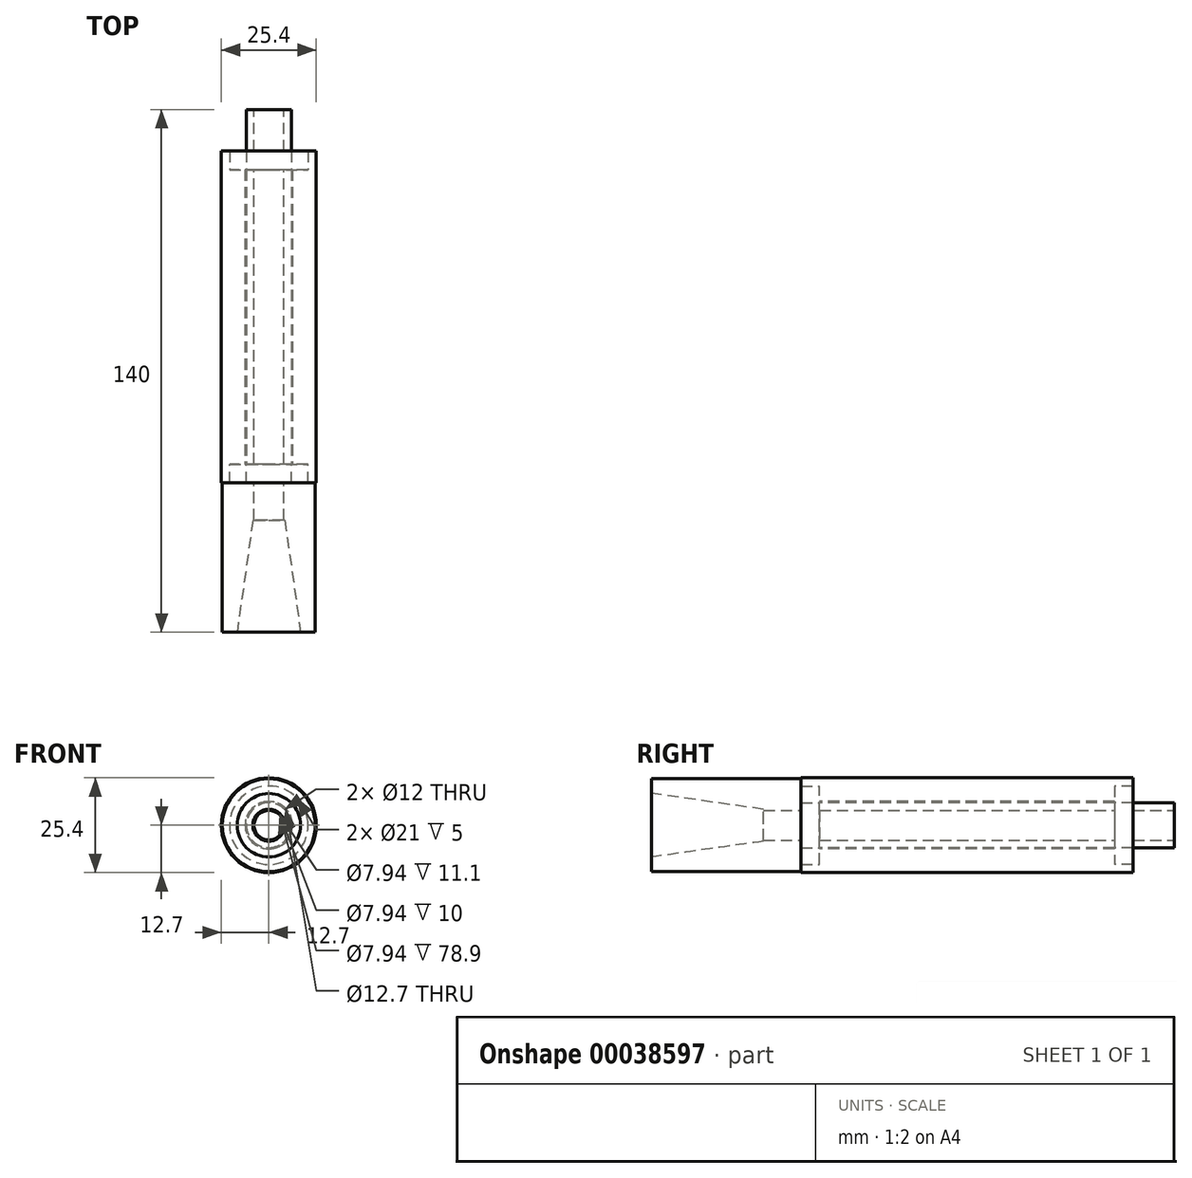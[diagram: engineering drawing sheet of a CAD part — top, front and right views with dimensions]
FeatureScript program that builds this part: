
annotation { "Feature Type Name" : "Feature", "Feature Type Description" : "" }
export const myFeature = defineFeature(function(context is Context, id is Id, definition is map)
    precondition{}
    {
        {
            var Q0;
            Q0=qCreatedBy(makeId("Front.planeOp"),FACE);
            var sketch = newSketch(context, id + "F0", { "sketchPlane" : qUnion([Q0])});
            skCircle(sketch, "E0", {"center": v(0, 0) * mm, "radius": 6.35 * mm});
            skCircle(sketch, "E1", {"center": v(0, 0) * mm, "radius": 12.7 * mm});
            skSolve(sketch);
        }
        {
            var Q0;
            Q0=makeQuery(id+"F0.imprint","IMPRINT",FACE,{"disambiguationData":[TD([[makeQuery(id+"F0.imprint","IMPRINT",EDGE,{"derivedFrom":sQuery(id+"F0.wireOp",EDGE,"E0")}),-1.0]])]});
            extrude(context, id + "F1", {"entities" : qUnion([Q0]), "oppositeDirection" : true, "depth" : 88.9 * mm});
        }
        {
            var Q0;
            Q0=qCreatedBy(makeId("Front.planeOp"),FACE);
            var sketch = newSketch(context, id + "F2", { "sketchPlane" : qUnion([Q0])});
            skCircle(sketch, "E2", {"center": v(0, 0) * mm, "radius": 12.45 * mm});
            skSolve(sketch);
        }
        {
            var Q0;
            Q0 = qSketchRegion(id + "F2", true);
            extrude(context, id + "F3", {"entities" : qUnion([Q0]), "depth" : 40 * mm});
        }
        {
            var Q0;
            Q0=makeQuery(id+"F3.opExtrude","CAP_FACE",FACE,{"disambiguationData":[OSD([sQuery(id+"F2.wireOp",EDGE,"E2")])],"isStart":false});
            var sketch = newSketch(context, id + "F4", { "sketchPlane" : qUnion([Q0])});
            skCircle(sketch, "E3", {"center": v(0, 0) * mm, "radius": 8.5 * mm});
            skSolve(sketch);
        }
        {
            var Q0;
            Q0 = qSketchRegion(id + "F4", true);
            extrude(context, id + "F5", {"entities" : qUnion([Q0]), "operationType" : NewBodyOperationType.REMOVE, "oppositeDirection" : true, "depth" : 30 * mm, "hasDraft" : true, "draftAngle" : 8 * degree, "draftPullDirection" : true});
        }
        {
            var Q0;
            Q0=makeQuery(id+"F3.opExtrude","CAP_FACE",FACE,{"disambiguationData":[OSD([sQuery(id+"F2.wireOp",EDGE,"E2")])],"isStart":true});
            var sketch = newSketch(context, id + "F6", { "sketchPlane" : qUnion([Q0])});
            skCircle(sketch, "E4", {"center": v(0, 0) * mm, "radius": 6 * mm});
            skSolve(sketch);
        }
        {
            var Q0;
            Q0 = qSketchRegion(id + "F6", true);
            extrude(context, id + "F7", {"entities" : qUnion([Q0]), "operationType" : NewBodyOperationType.ADD, "depth" : 100 * mm});
        }
        {
            var Q0;
            Q0=makeQuery(id+"F7.opExtrude","CAP_FACE",FACE,{"disambiguationData":[OSD([sQuery(id+"F6.wireOp",EDGE,"E4")])],"isStart":false});
            var sketch = newSketch(context, id + "F8", { "sketchPlane" : qUnion([Q0])});
            skCircle(sketch, "E5", {"center": v(0, 0) * mm, "radius": 3.97 * mm});
            skSolve(sketch);
        }
        {
            var Q0;
            Q0 = qSketchRegion(id + "F8", true);
            extrude(context, id + "F9", {"entities" : qUnion([Q0]), "operationType" : NewBodyOperationType.REMOVE, "endBound" : BoundingType.THROUGH_ALL, "oppositeDirection" : true, "depth" : 25.4 * mm});
        }
        {
            var Q0;
            Q0=makeQuery(id+"F1.opExtrude","CAP_FACE",FACE,{"disambiguationData":[OSD([sQuery(id+"F0.wireOp",EDGE,"E0"),sQuery(id+"F0.wireOp",EDGE,"E1")])],"isStart":true});
            var sketch = newSketch(context, id + "F10", { "sketchPlane" : qUnion([Q0])});
            skCircle(sketch, "E6", {"center": v(0, 0) * mm, "radius": 10.5 * mm});
            skSolve(sketch);
        }
        {
            var Q0;
            Q0 = qSketchRegion(id + "F10", true);
            extrude(context, id + "F11", {"entities" : qUnion([Q0]), "operationType" : NewBodyOperationType.REMOVE, "oppositeDirection" : true, "depth" : 5 * mm});
        }
        {
            var Q0;
            Q0=makeQuery(id+"F11.boolean.opBoolean","COPY",FACE,{"derivedFrom":makeQuery(id+"F11.opExtrude","CAP_FACE",FACE,{"disambiguationData":[OSD([sQuery(id+"F10.wireOp",EDGE,"E6")])],"isStart":false})});
            var sketch = newSketch(context, id + "F12", { "sketchPlane" : qUnion([Q0])});
            skCircle(sketch, "E7", {"center": v(0, 0) * mm, "radius": 10.5 * mm});
            skCircle(sketch, "E8", {"center": v(0, 0) * mm, "radius": 6 * mm});
            skSolve(sketch);
        }
        {
            var Q0;
            Q0 = qSketchRegion(id + "F12", true);
            extrude(context, id + "F13", {"entities" : qUnion([Q0]), "depth" : 5 * mm});
        }
        {
            var Q0;
            Q0=makeQuery(id+"F1.opExtrude","CAP_FACE",FACE,{"disambiguationData":[OSD([sQuery(id+"F0.wireOp",EDGE,"E0"),sQuery(id+"F0.wireOp",EDGE,"E1")])],"isStart":false});
            var sketch = newSketch(context, id + "F14", { "sketchPlane" : qUnion([Q0])});
            skCircle(sketch, "E9", {"center": v(0, 0) * mm, "radius": 10.5 * mm});
            skSolve(sketch);
        }
        {
            var Q0;
            Q0 = qSketchRegion(id + "F14", true);
            extrude(context, id + "F15", {"entities" : qUnion([Q0]), "operationType" : NewBodyOperationType.REMOVE, "oppositeDirection" : true, "depth" : 5 * mm});
        }
        {
            var Q0;
            Q0=makeQuery(id+"F15.boolean.opBoolean","COPY",FACE,{"derivedFrom":makeQuery(id+"F15.opExtrude","CAP_FACE",FACE,{"disambiguationData":[OSD([sQuery(id+"F14.wireOp",EDGE,"E9")])],"isStart":false})});
            var sketch = newSketch(context, id + "F16", { "sketchPlane" : qUnion([Q0])});
            skCircle(sketch, "E10", {"center": v(0, 0) * mm, "radius": 10.5 * mm});
            skCircle(sketch, "E11", {"center": v(0, 0) * mm, "radius": 6 * mm});
            skSolve(sketch);
        }
        {
            var Q0;
            Q0 = qSketchRegion(id + "F16", true);
            extrude(context, id + "F17", {"entities" : qUnion([Q0]), "depth" : 5 * mm});
        }
    });
